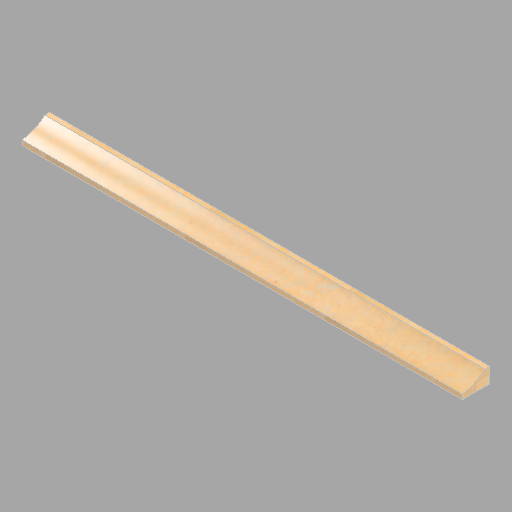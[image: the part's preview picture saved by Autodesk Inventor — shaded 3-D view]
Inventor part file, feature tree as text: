
AUTODESK INVENTOR PART (.ipt)
format: ipt  version: 2022.2 (Build 262287010, 287A)  size: 175,104 bytes
history: native  units: in
note: dims shown in document units (in); Inventor stores cm internally (conversion verified against a paired STEP export)
features: revolve x2, direct_edit x1
ambient origin geometry x8: Origin, YZ Plane, XZ Plane, XY Plane, X Axis, Y Axis, Z Axis, Center Point
bodies: Solid1 (feature_tree), Body1 (feature_tree)
feature tree (3):
  direct_edit  "Direct Edit1"
  revolve  "Rotate1"  [1 undecoded]
  revolve  "Rotate2"  [1 undecoded]
note: 2 required parameter values undecoded (feature->parameter linkage not recoverable at this tier; creation-order binding heuristic only, values carry confidence <= 0.55)
